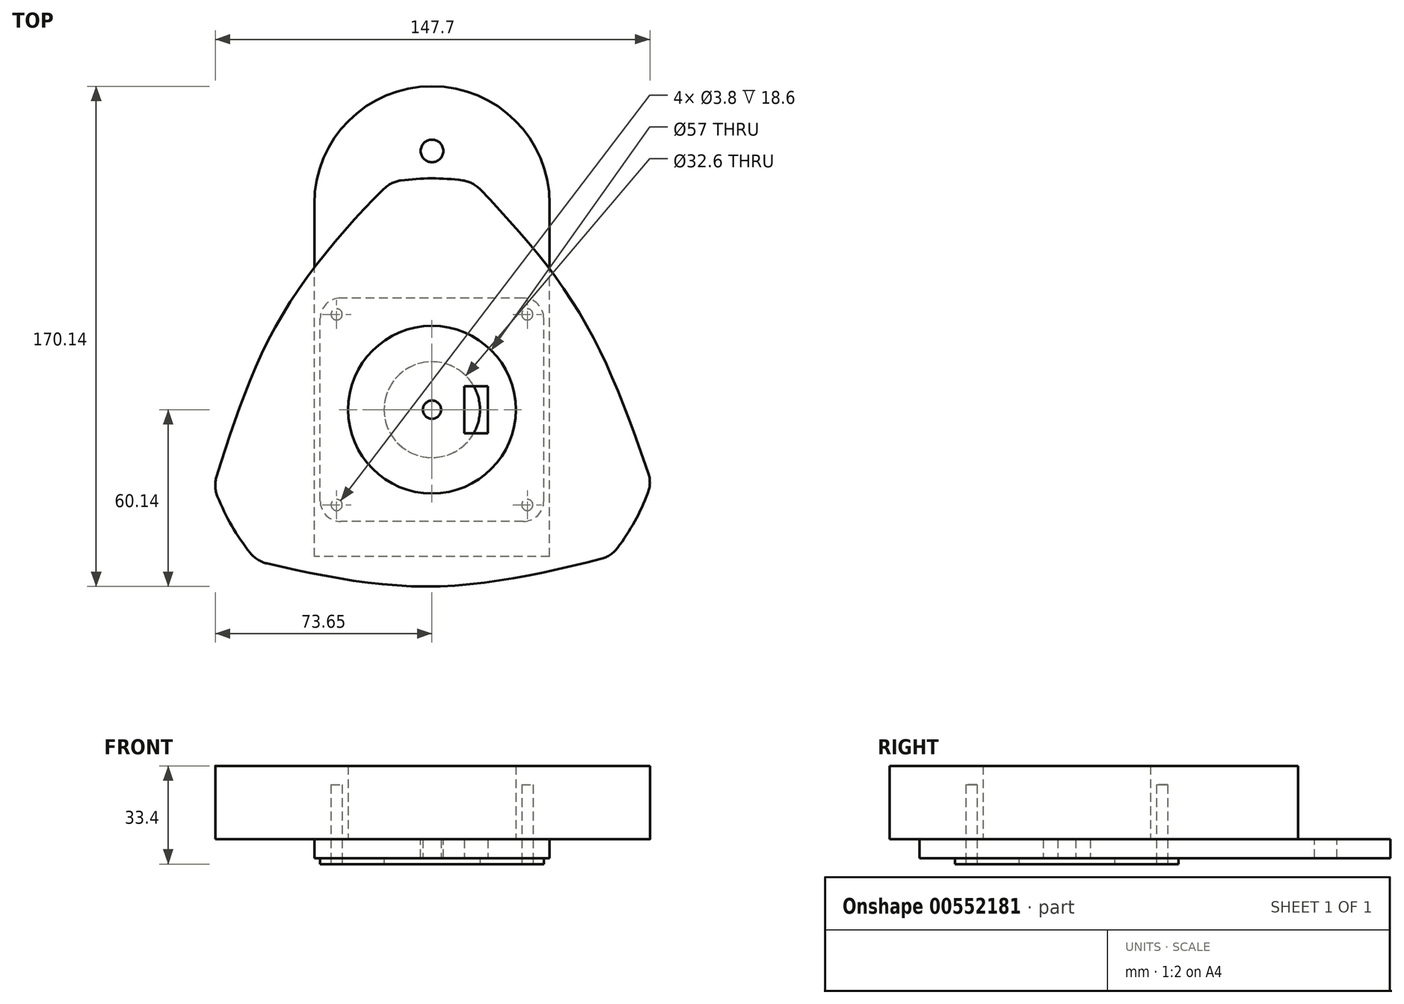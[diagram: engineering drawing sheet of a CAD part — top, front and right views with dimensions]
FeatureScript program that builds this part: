
annotation { "Feature Type Name" : "Feature", "Feature Type Description" : "" }
export const myFeature = defineFeature(function(context is Context, id is Id, definition is map)
    precondition{}
    {
        {
            var Q0;
            Q0=qCreatedBy(makeId("Top.planeOp"),FACE);
            var sketch = newSketch(context, id + "F0", { "sketchPlane" : qUnion([Q0])});
            skCircle(sketch, "E0", {"center": v(0, 0) * mm, "radius": 28.5 * mm});
            skLineSegment(sketch, "E1.bottom", {"start": v(38.16, -43.24) * mm, "end": v(-38.04, -43.24) * mm});
            skLineSegment(sketch, "E1.top", {"start": v(38.16, 32.96) * mm, "end": v(-38.04, 32.96) * mm});
            skLineSegment(sketch, "E1.left", {"start": v(38.16, -43.24) * mm, "end": v(38.16, 32.96) * mm});
            skLineSegment(sketch, "E1.right", {"start": v(-38.04, -43.24) * mm, "end": v(-38.04, 32.96) * mm});
            skPoint(sketch, "E1.middle", {"position": v(0.06, -5.14) * mm});
            skCircle(sketch, "E2", {"center": v(-32.4, 27.31) * mm, "radius": 1.95 * mm});
            skCircle(sketch, "E3", {"center": v(32.5, 27.31) * mm, "radius": 1.95 * mm});
            skCircle(sketch, "E4", {"center": v(32.5, -37.59) * mm, "radius": 1.95 * mm});
            skCircle(sketch, "E5", {"center": v(-32.4, -37.59) * mm, "radius": 1.95 * mm});
            skSolve(sketch);
        }
        {
            var Q0;
            Q0=qCreatedBy(makeId("Top.planeOp"),FACE);
            var sketch = newSketch(context, id + "F1", { "sketchPlane" : qUnion([Q0])});
            skFitSpline(sketch, "E6", {"points": [v(-74.29, -26.22) * mm, v(-52.16, 30.04) * mm, v(-13.96, 77.42) * mm], "startDerivative": vector(36.92, 116.05) * mm, "endDerivative": vector(81.24, 78.34) * mm});
            skFitSpline(sketch, "E7", {"points": [v(13.96, 77.42) * mm, v(51.24, 31) * mm, v(74.65, -24.8) * mm], "startDerivative": vector(83.92, -86.38) * mm, "endDerivative": vector(39.7, -114.15) * mm});
            skFitSpline(sketch, "E8", {"points": [v(-59.62, -51.47) * mm, v(0, -60.13) * mm, v(60.84, -49.87) * mm], "startDerivative": vector(119.87, -28.02) * mm, "endDerivative": vector(119.63, 30.4) * mm});
            skArc(sketch, "E9", {"start": v(-72.92, -29.52) * mm, "mid": v(-68.02, -39.52) * mm, "end": v(-61.76, -48.73) * mm});
            skArc(sketch, "E10.trimOffspring", {"start": v(10.42, 77.97) * mm, "mid": v(-0.1, 78.66) * mm, "end": v(-10.6, 77.95) * mm});
            skArc(sketch, "E11.trimOffspring", {"start": v(63.09, -46.99) * mm, "mid": v(68.87, -38.02) * mm, "end": v(73.38, -28.36) * mm});
            skArc(sketch, "E12.filletArc", {"start": v(-10.6, 77.95) * mm, "mid": v(-13.67, 77.01) * mm, "end": v(-16.28, 75.16) * mm});
            skArc(sketch, "E13.filletArc", {"start": v(16.3, 74.99) * mm, "mid": v(13.62, 76.98) * mm, "end": v(10.42, 77.97) * mm});
            skArc(sketch, "E14.filletArc", {"start": v(73.38, -28.36) * mm, "mid": v(74.05, -24.92) * mm, "end": v(73.5, -21.47) * mm});
            skArc(sketch, "E15.filletArc", {"start": v(57.51, -50.71) * mm, "mid": v(60.62, -49.33) * mm, "end": v(63.09, -46.99) * mm});
            skPoint(sketch, "E16.visualSharp", {"position": v(-59.45, -51.51) * mm});
            skArc(sketch, "E16.filletArc", {"start": v(-61.76, -48.73) * mm, "mid": v(-59.26, -50.98) * mm, "end": v(-56.16, -52.28) * mm});
            skArc(sketch, "E17.filletArc", {"start": v(-73.18, -22.74) * mm, "mid": v(-73.64, -26.15) * mm, "end": v(-72.92, -29.52) * mm});
            skSolve(sketch);
        }
        {
            var Q0;
            Q0 = qSketchRegion(id + "F1", true);
            extrude(context, id + "F2", {"entities" : qUnion([Q0]), "depth" : 25 * mm, "offsetDistance" : 25 * mm});
        }
        {
            var Q0;
            Q0=makeQuery(id+"F0.imprint","IMPRINT",FACE,{"disambiguationData":[TD([[makeQuery(id+"F0.imprint","IMPRINT",EDGE,{"derivedFrom":sQuery(id+"F0.wireOp",EDGE,"E0")}),1.0]])]});
            var Q1;
            Q1=sQuery(id+"F0.wireOp",EDGE,"E0");
            extrude(context, id + "F3", {"entities" : qUnion([Q0]), "operationType" : NewBodyOperationType.REMOVE, "surfaceEntities" : qUnion([Q1]), "depth" : 25 * mm, "offsetDistance" : 25 * mm});
        }
        {
            var Q0;
            Q0=qCreatedBy(makeId("Top.planeOp"),FACE);
            var sketch = newSketch(context, id + "F4", { "sketchPlane" : qUnion([Q0])});
            skLineSegment(sketch, "E18.bottom", {"start": v(31, -38) * mm, "end": v(-31, -38) * mm});
            skLineSegment(sketch, "E18.top", {"start": v(31, 38) * mm, "end": v(-31, 38) * mm});
            skLineSegment(sketch, "E18.left", {"start": v(38, -31) * mm, "end": v(38, 31) * mm});
            skLineSegment(sketch, "E18.right", {"start": v(-38, -31) * mm, "end": v(-38, 31) * mm});
            skPoint(sketch, "E18.middle", {"position": v(0, 0) * mm});
            skCircle(sketch, "E19", {"center": v(0, 0) * mm, "radius": 16.3 * mm});
            skCircle(sketch, "E20", {"center": v(-32.4, 32.4) * mm, "radius": 1.9 * mm});
            skCircle(sketch, "E21", {"center": v(32.4, 32.4) * mm, "radius": 1.9 * mm});
            skCircle(sketch, "E22", {"center": v(32.4, -32.4) * mm, "radius": 1.9 * mm});
            skCircle(sketch, "E23", {"center": v(-32.4, -32.4) * mm, "radius": 1.9 * mm});
            skPoint(sketch, "E24.visualSharp", {"position": v(38, 38) * mm});
            skArc(sketch, "E24.filletArc", {"start": v(38, 31) * mm, "mid": v(35.95, 35.95) * mm, "end": v(31, 38) * mm});
            skPoint(sketch, "E25.visualSharp", {"position": v(38, -38) * mm});
            skArc(sketch, "E25.filletArc", {"start": v(31, -38) * mm, "mid": v(35.95, -35.95) * mm, "end": v(38, -31) * mm});
            skPoint(sketch, "E26.visualSharp", {"position": v(-38, -38) * mm});
            skArc(sketch, "E26.filletArc", {"start": v(-38, -31) * mm, "mid": v(-35.95, -35.95) * mm, "end": v(-31, -38) * mm});
            skPoint(sketch, "E27.visualSharp", {"position": v(-38, 38) * mm});
            skArc(sketch, "E27.filletArc", {"start": v(-31, 38) * mm, "mid": v(-35.95, 35.95) * mm, "end": v(-38, 31) * mm});
            skSolve(sketch);
        }
        {
            var Q0;
            Q0=makeQuery(id+"F4.imprint","IMPRINT",FACE,{"disambiguationData":[TD([[makeQuery(id+"F4.imprint","IMPRINT",EDGE,{"derivedFrom":sQuery(id+"F4.wireOp",EDGE,"E18.bottom")}),-1.0]])]});
            extrude(context, id + "F5", {"entities" : qUnion([Q0]), "depth" : 2 * mm, "offsetDistance" : 25 * mm});
        }
        {
            var Q0;
            Q0=qCreatedBy(makeId("Top.planeOp"),FACE);
            var sketch = newSketch(context, id + "F6", { "sketchPlane" : qUnion([Q0])});
            skLineSegment(sketch, "E28.bottom", {"start": v(40, -80) * mm, "end": v(-40, -80) * mm});
            skLineSegment(sketch, "E28.top", {"start": v(0, 80) * mm, "end": v(0, 80) * mm});
            skLineSegment(sketch, "E28.left", {"start": v(40, -80) * mm, "end": v(40, 40) * mm});
            skLineSegment(sketch, "E28.right", {"start": v(-40, -80) * mm, "end": v(-40, 40) * mm});
            skPoint(sketch, "E28.middle", {"position": v(0, 0) * mm});
            skPoint(sketch, "E29.visualSharp", {"position": v(-40, 80) * mm});
            skArc(sketch, "E29.filletArc", {"start": v(0, 80) * mm, "mid": v(-28.28, 68.28) * mm, "end": v(-40, 40) * mm});
            skPoint(sketch, "E30.visualSharp", {"position": v(40, 80) * mm});
            skArc(sketch, "E30.filletArc", {"start": v(40, 40) * mm, "mid": v(28.28, 68.28) * mm, "end": v(0, 80) * mm});
            skSolve(sketch);
        }
        {
            var Q0;
            Q0=makeQuery(id+"F6.imprint","IMPRINT",FACE,{"disambiguationData":[TD([[makeQuery(id+"F6.imprint","IMPRINT",EDGE,{"derivedFrom":sQuery(id+"F6.wireOp",EDGE,"E28.bottom")}),-1.0]])]});
            extrude(context, id + "F7", {"entities" : qUnion([Q0]), "depth" : 6.4 * mm, "offsetDistance" : 25 * mm});
        }
        {
            var Q0;
            Q0=makeQuery(id+"F7.opExtrude","SWEPT_BODY",BODY,{"disambiguationData":[OSD([sQuery(id+"F6.wireOp",EDGE,"E28.bottom"),sQuery(id+"F6.wireOp",EDGE,"E28.left"),sQuery(id+"F6.wireOp",EDGE,"E28.right"),sQuery(id+"F6.wireOp",EDGE,"E29.filletArc"),sQuery(id+"F6.wireOp",EDGE,"E30.filletArc")])]});
            var Q1;
            Q1=makeQuery(id+"F7.opExtrude","SWEPT_EDGE",EDGE,{"disambiguationData":[OSD([sQuery(id+"F6.wireOp",EDGE,"E28.left"),sQuery(id+"F6.wireOp",EDGE,"E30.filletArc")])]});
            transform(context, id + "F8", {"entities" : qUnion([Q0]), "transformType" : TransformType.TRANSLATION_ENTITY, "oppositeDirectionEntity" : false, "transformLine" : qUnion([Q1]), "makeCopy" : false});
        }
        {
            var Q0;
            Q0=makeQuery(id+"F7.opExtrude","SWEPT_BODY",BODY,{"disambiguationData":[OSD([sQuery(id+"F6.wireOp",EDGE,"E28.bottom"),sQuery(id+"F6.wireOp",EDGE,"E28.left"),sQuery(id+"F6.wireOp",EDGE,"E28.right"),sQuery(id+"F6.wireOp",EDGE,"E29.filletArc"),sQuery(id+"F6.wireOp",EDGE,"E30.filletArc")])]});
            var Q1;
            Q1=makeQuery(id+"F5.opExtrude","CAP_EDGE",EDGE,{"disambiguationData":[OSD([sQuery(id+"F4.wireOp",EDGE,"E18.left")])],"isStart":false});
            transform(context, id + "F9", {"entities" : qUnion([Q0]), "transformType" : TransformType.TRANSLATION_DISTANCE, "transformDirection" : qUnion([Q1]), "distance" : 40 * mm, "makeCopy" : false});
        }
        {
            var Q0;
            Q0=makeQuery(id+"F5.opExtrude","SWEPT_BODY",BODY,{"disambiguationData":[OSD([sQuery(id+"F4.wireOp",EDGE,"E18.bottom"),sQuery(id+"F4.wireOp",EDGE,"E18.top"),sQuery(id+"F4.wireOp",EDGE,"E18.left"),sQuery(id+"F4.wireOp",EDGE,"E18.right"),sQuery(id+"F4.wireOp",EDGE,"E19"),sQuery(id+"F4.wireOp",EDGE,"E20"),sQuery(id+"F4.wireOp",EDGE,"E21"),sQuery(id+"F4.wireOp",EDGE,"E22"),sQuery(id+"F4.wireOp",EDGE,"E23"),sQuery(id+"F4.wireOp",EDGE,"E24.filletArc"),sQuery(id+"F4.wireOp",EDGE,"E25.filletArc"),sQuery(id+"F4.wireOp",EDGE,"E26.filletArc"),sQuery(id+"F4.wireOp",EDGE,"E27.filletArc")])]});
            transform(context, id + "F10", {"entities" : qUnion([Q0]), "transformType" : TransformType.TRANSLATION_3D, "dx" : 0 * mm, "dy" : 0 * mm, "dz" : -2 * mm, "makeCopy" : false});
        }
        {
            var Q0;
            Q0=makeQuery(id+"F5.opExtrude","SWEPT_BODY",BODY,{"disambiguationData":[OSD([sQuery(id+"F4.wireOp",EDGE,"E18.bottom"),sQuery(id+"F4.wireOp",EDGE,"E18.top"),sQuery(id+"F4.wireOp",EDGE,"E18.left"),sQuery(id+"F4.wireOp",EDGE,"E18.right"),sQuery(id+"F4.wireOp",EDGE,"E19"),sQuery(id+"F4.wireOp",EDGE,"E20"),sQuery(id+"F4.wireOp",EDGE,"E21"),sQuery(id+"F4.wireOp",EDGE,"E22"),sQuery(id+"F4.wireOp",EDGE,"E23"),sQuery(id+"F4.wireOp",EDGE,"E24.filletArc"),sQuery(id+"F4.wireOp",EDGE,"E25.filletArc"),sQuery(id+"F4.wireOp",EDGE,"E26.filletArc"),sQuery(id+"F4.wireOp",EDGE,"E27.filletArc")])]});
            transform(context, id + "F11", {"entities" : qUnion([Q0]), "transformType" : TransformType.TRANSLATION_3D, "dx" : 0 * mm, "dy" : 0 * mm, "dz" : -6.4 * mm, "makeCopy" : false});
        }
        {
            var Q0;
            Q0=makeQuery(id+"F7.opExtrude","SWEPT_BODY",BODY,{"disambiguationData":[OSD([sQuery(id+"F6.wireOp",EDGE,"E28.bottom"),sQuery(id+"F6.wireOp",EDGE,"E28.left"),sQuery(id+"F6.wireOp",EDGE,"E28.right"),sQuery(id+"F6.wireOp",EDGE,"E29.filletArc"),sQuery(id+"F6.wireOp",EDGE,"E30.filletArc")])]});
            transform(context, id + "F12", {"entities" : qUnion([Q0]), "transformType" : TransformType.TRANSLATION_3D, "dx" : 0 * mm, "dy" : -10 * mm, "dz" : 0 * mm, "makeCopy" : false});
        }
        {
            var Q0;
            Q0=qCreatedBy(makeId("Top.planeOp"),FACE);
            var sketch = newSketch(context, id + "F13", { "sketchPlane" : qUnion([Q0])});
            skCircle(sketch, "E31", {"center": v(0, 88) * mm, "radius": 3.85 * mm});
            skSolve(sketch);
        }
        {
            var Q0;
            Q0=makeQuery(id+"F13.imprint","IMPRINT",FACE,{"disambiguationData":[TD([[makeQuery(id+"F13.imprint","IMPRINT",EDGE,{"derivedFrom":sQuery(id+"F13.wireOp",EDGE,"E31")}),1.0]])]});
            extrude(context, id + "F14", {"entities" : qUnion([Q0]), "operationType" : NewBodyOperationType.REMOVE, "oppositeDirection" : true, "depth" : 25 * mm, "offsetDistance" : 25 * mm});
        }
        {
            var Q0;
            Q0=makeQuery(id+"F7.opExtrude","CAP_FACE",FACE,{"disambiguationData":[OSD([sQuery(id+"F6.wireOp",EDGE,"E28.bottom"),sQuery(id+"F6.wireOp",EDGE,"E28.left"),sQuery(id+"F6.wireOp",EDGE,"E28.right"),sQuery(id+"F6.wireOp",EDGE,"E29.filletArc"),sQuery(id+"F6.wireOp",EDGE,"E30.filletArc")])],"isStart":true});
            var sketch = newSketch(context, id + "F15", { "sketchPlane" : qUnion([Q0])});
            skCircle(sketch, "E32", {"center": v(-32.4, 32.4) * mm, "radius": 1.9 * mm});
            skCircle(sketch, "E33", {"center": v(32.4, 32.4) * mm, "radius": 1.9 * mm});
            skCircle(sketch, "E34", {"center": v(32.4, -32.4) * mm, "radius": 1.9 * mm});
            skCircle(sketch, "E35", {"center": v(-32.4, -32.4) * mm, "radius": 1.9 * mm});
            skCircle(sketch, "E36", {"center": v(0, 0) * mm, "radius": 3.1 * mm});
            skLineSegment(sketch, "E37.bottom", {"start": v(19, -8) * mm, "end": v(11, -8) * mm});
            skLineSegment(sketch, "E37.top", {"start": v(19, 8) * mm, "end": v(11, 8) * mm});
            skLineSegment(sketch, "E37.left", {"start": v(19, -8) * mm, "end": v(19, 8) * mm});
            skLineSegment(sketch, "E37.right", {"start": v(11, -8) * mm, "end": v(11, 8) * mm});
            skPoint(sketch, "E37.middle", {"position": v(15, 0) * mm});
            skSolve(sketch);
        }
        {
            var Q0;
            Q0=makeQuery(id+"F15.imprint","IMPRINT",FACE,{"disambiguationData":[TD([[makeQuery(id+"F15.imprint","IMPRINT",EDGE,{"derivedFrom":sQuery(id+"F15.wireOp",EDGE,"E32")}),1.0]])]});
            var Q1;
            Q1=makeQuery(id+"F15.imprint","IMPRINT",FACE,{"disambiguationData":[TD([[makeQuery(id+"F15.imprint","IMPRINT",EDGE,{"derivedFrom":sQuery(id+"F15.wireOp",EDGE,"E33")}),1.0]])]});
            var Q2;
            Q2=makeQuery(id+"F15.imprint","IMPRINT",FACE,{"disambiguationData":[TD([[makeQuery(id+"F15.imprint","IMPRINT",EDGE,{"derivedFrom":sQuery(id+"F15.wireOp",EDGE,"E34")}),1.0]])]});
            var Q3;
            Q3=makeQuery(id+"F15.imprint","IMPRINT",FACE,{"disambiguationData":[TD([[makeQuery(id+"F15.imprint","IMPRINT",EDGE,{"derivedFrom":sQuery(id+"F15.wireOp",EDGE,"E35")}),1.0]])]});
            var Q4;
            Q4=makeQuery(id+"F15.imprint","IMPRINT",FACE,{"disambiguationData":[TD([[makeQuery(id+"F15.imprint","IMPRINT",EDGE,{"derivedFrom":sQuery(id+"F15.wireOp",EDGE,"E37.bottom")}),-1.0]])]});
            var Q5;
            Q5=sQuery(id+"F15.wireOp",EDGE,"E32");
            var Q6;
            Q6=sQuery(id+"F15.wireOp",EDGE,"E33");
            var Q7;
            Q7=sQuery(id+"F15.wireOp",EDGE,"E34");
            var Q8;
            Q8=sQuery(id+"F15.wireOp",EDGE,"E35");
            extrude(context, id + "F16", {"entities" : qUnion([Q0, Q1, Q2, Q3, Q4]), "operationType" : NewBodyOperationType.REMOVE, "surfaceEntities" : qUnion([Q5, Q6, Q7, Q8]), "oppositeDirection" : true, "depth" : 25 * mm, "offsetDistance" : 25 * mm});
        }
        {
            var Q0;
            Q0=makeQuery(id+"F15.imprint","IMPRINT",FACE,{"disambiguationData":[TD([[makeQuery(id+"F15.imprint","IMPRINT",EDGE,{"derivedFrom":sQuery(id+"F15.wireOp",EDGE,"E36")}),1.0]])]});
            var Q1;
            Q1=sQuery(id+"F15.wireOp",EDGE,"E36");
            extrude(context, id + "F17", {"entities" : qUnion([Q0]), "operationType" : NewBodyOperationType.REMOVE, "surfaceEntities" : qUnion([Q1]), "oppositeDirection" : true, "depth" : 25 * mm, "offsetDistance" : 25 * mm});
        }
    });
